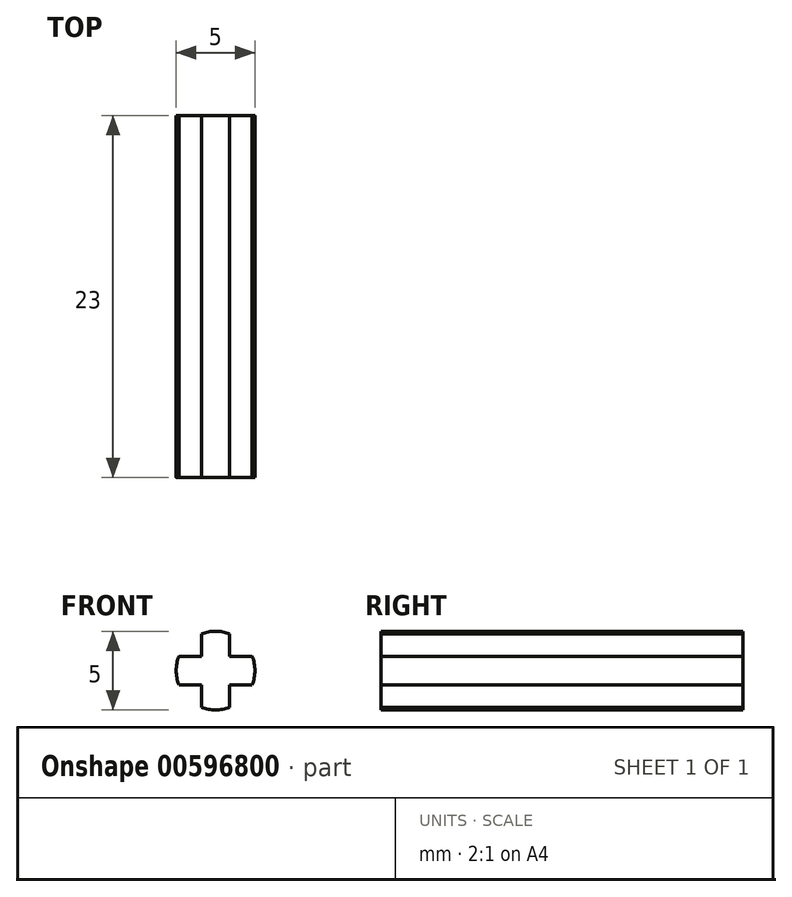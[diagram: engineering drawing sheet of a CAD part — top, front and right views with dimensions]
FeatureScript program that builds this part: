
annotation { "Feature Type Name" : "Feature", "Feature Type Description" : "" }
export const myFeature = defineFeature(function(context is Context, id is Id, definition is map)
    precondition{}
    {
        {
            var Q0;
            Q0=qCreatedBy(makeId("Front.planeOp"),FACE);
            var sketch = newSketch(context, id + "F0", { "sketchPlane" : qUnion([Q0])});
            skArc(sketch, "E0", {"start": v(2.33, -0.9) * mm, "mid": v(2.5, 0) * mm, "end": v(2.33, 0.9) * mm});
            skLineSegment(sketch, "E1.left", {"start": v(-0.9, 2.33) * mm, "end": v(-0.9, 0.9) * mm});
            skLineSegment(sketch, "E1.right", {"start": v(0.9, 2.33) * mm, "end": v(0.9, 0.9) * mm});
            skLineSegment(sketch, "E2.bottom", {"start": v(2.33, 0.9) * mm, "end": v(0.9, 0.9) * mm});
            skLineSegment(sketch, "E2.top", {"start": v(2.33, -0.9) * mm, "end": v(0.9, -0.9) * mm});
            skPoint(sketch, "E3.orphan", {"position": v(-3.61, -0.9) * mm});
            skPoint(sketch, "E1.top.start.orphan", {"position": v(-0.9, -3.45) * mm});
            skPoint(sketch, "E4.orphan", {"position": v(0.9, -3.45) * mm});
            skPoint(sketch, "E2.left.end.orphan", {"position": v(3.61, -0.9) * mm});
            skPoint(sketch, "E5.orphan", {"position": v(3.61, 0.9) * mm});
            skArc(sketch, "E6.trimOffspring", {"start": v(0.9, 2.33) * mm, "mid": v(0, 2.5) * mm, "end": v(-0.9, 2.33) * mm});
            skPoint(sketch, "E1.bottom.end.orphan", {"position": v(0.9, 3.45) * mm});
            skPoint(sketch, "E7.orphan", {"position": v(-0.9, 3.45) * mm});
            skArc(sketch, "E8.trimOffspring", {"start": v(-2.33, 0.9) * mm, "mid": v(-2.5, 0) * mm, "end": v(-2.33, -0.9) * mm});
            skArc(sketch, "E9.trimOffspring", {"start": v(-0.9, -2.33) * mm, "mid": v(0, -2.5) * mm, "end": v(0.9, -2.33) * mm});
            skPoint(sketch, "E10.orphan", {"position": v(-3.61, 0.9) * mm});
            skLineSegment(sketch, "E11.trimOffspring", {"start": v(-0.9, -0.9) * mm, "end": v(-0.9, -2.33) * mm});
            skLineSegment(sketch, "E12.trimOffspring", {"start": v(-0.9, 0.9) * mm, "end": v(-2.33, 0.9) * mm});
            skLineSegment(sketch, "E13.trimOffspring", {"start": v(0.9, -0.9) * mm, "end": v(0.9, -2.33) * mm});
            skLineSegment(sketch, "E14.trimOffspring", {"start": v(-0.9, -0.9) * mm, "end": v(-2.33, -0.9) * mm});
            skSolve(sketch);
        }
        {
            var Q0;
            Q0=qSketchRegion(id+"F0",true);
            extrude(context, id + "F1", {"entities" : qUnion([Q0]), "endBound" : BoundingType.SYMMETRIC, "depth" : 23 * mm, "offsetDistance" : 25 * mm});
        }
    });
